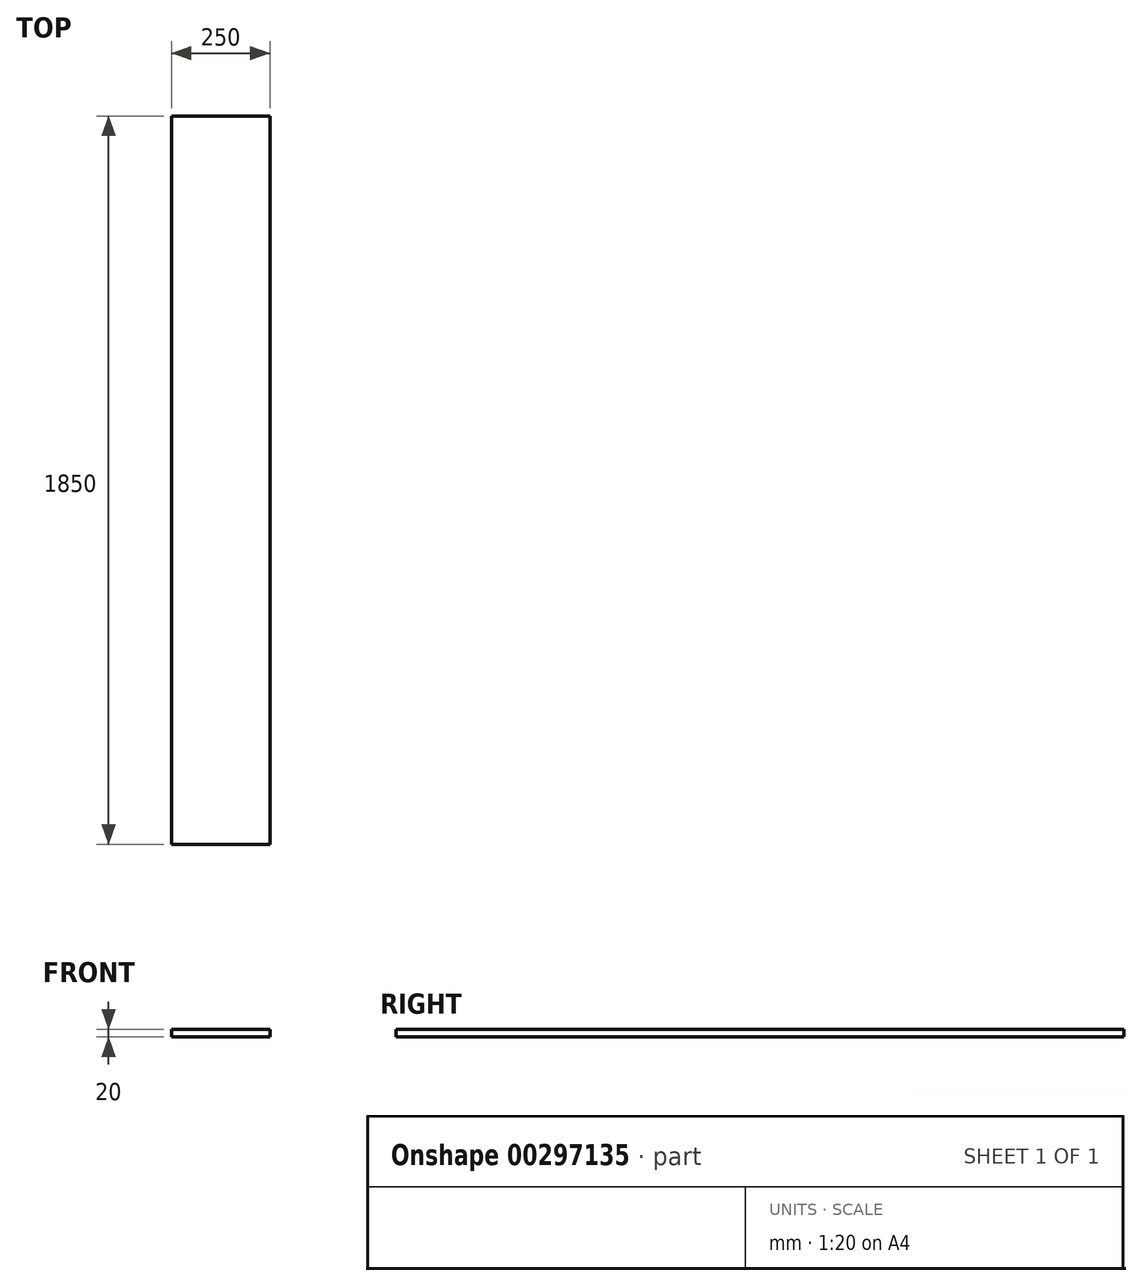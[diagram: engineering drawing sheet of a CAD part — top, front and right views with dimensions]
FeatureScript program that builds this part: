
annotation { "Feature Type Name" : "Feature", "Feature Type Description" : "" }
export const myFeature = defineFeature(function(context is Context, id is Id, definition is map)
    precondition{}
    {
        {
            var Q0;
            Q0=qCreatedBy(makeId("Top.planeOp"),FACE);
            var sketch = newSketch(context, id + "F0", { "sketchPlane" : qUnion([Q0])});
            skLineSegment(sketch, "E0.bottom", {"start": v(125, 925) * mm, "end": v(-125, 925) * mm});
            skLineSegment(sketch, "E0.top", {"start": v(125, -925) * mm, "end": v(-125, -925) * mm});
            skLineSegment(sketch, "E0.left", {"start": v(125, 925) * mm, "end": v(125, -925) * mm});
            skLineSegment(sketch, "E0.right", {"start": v(-125, 925) * mm, "end": v(-125, -925) * mm});
            skPoint(sketch, "E0.middle", {"position": v(0, 0) * mm});
            skSolve(sketch);
        }
        {
            var Q0;
            Q0 = qSketchRegion(id + "F0", true);
            extrude(context, id + "F1", {"entities" : qUnion([Q0]), "endBound" : BoundingType.SYMMETRIC, "depth" : 20 * mm});
        }
    });
